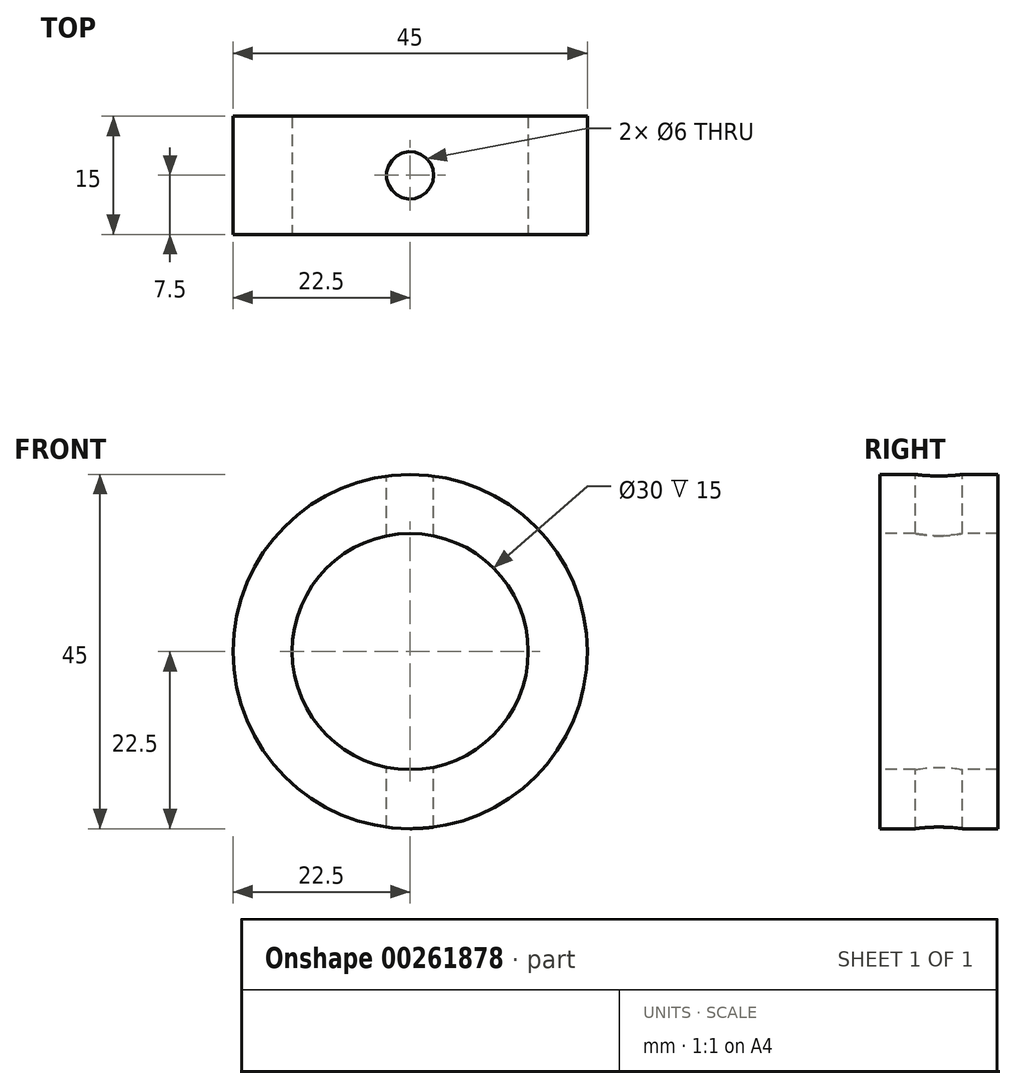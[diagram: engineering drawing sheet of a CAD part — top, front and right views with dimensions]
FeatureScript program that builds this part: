
annotation { "Feature Type Name" : "Feature", "Feature Type Description" : "" }
export const myFeature = defineFeature(function(context is Context, id is Id, definition is map)
    precondition{}
    {
        {
            var Q0;
            Q0=qCreatedBy(makeId("Front.planeOp"),FACE);
            var sketch = newSketch(context, id + "F0", { "sketchPlane" : qUnion([Q0])});
            skCircle(sketch, "E0", {"center": v(0, 0) * mm, "radius": 15 * mm});
            skCircle(sketch, "E1", {"center": v(0, 0) * mm, "radius": 22.5 * mm});
            skSolve(sketch);
        }
        {
            var Q0;
            Q0=makeQuery(id+"F0.imprint","IMPRINT",FACE,{"disambiguationData":[TD([[makeQuery(id+"F0.imprint","IMPRINT",EDGE,{"derivedFrom":sQuery(id+"F0.wireOp",EDGE,"E0")}),1.0]])]});
            var Q1;
            Q1=makeQuery(id+"F0.imprint","IMPRINT",FACE,{"disambiguationData":[TD([[makeQuery(id+"F0.imprint","IMPRINT",EDGE,{"derivedFrom":sQuery(id+"F0.wireOp",EDGE,"E0")}),-1.0]])]});
            extrude(context, id + "F1", {"entities" : qUnion([Q0, Q1]), "oppositeDirection" : true, "depth" : 15 * mm});
        }
        {
            var Q0;
            Q0=makeQuery(id+"F0.imprint","IMPRINT",FACE,{"disambiguationData":[TD([[makeQuery(id+"F0.imprint","IMPRINT",EDGE,{"derivedFrom":sQuery(id+"F0.wireOp",EDGE,"E0")}),1.0]])]});
            extrude(context, id + "F2", {"entities" : qUnion([Q0]), "operationType" : NewBodyOperationType.REMOVE, "endBound" : BoundingType.THROUGH_ALL, "oppositeDirection" : true, "depth" : 25 * mm});
        }
        {
            var Q0;
            Q0=qCreatedBy(makeId("Top.planeOp"),FACE);
            var sketch = newSketch(context, id + "F3", { "sketchPlane" : qUnion([Q0])});
            skCircle(sketch, "E2", {"center": v(0, 7.5) * mm, "radius": 3 * mm});
            skSolve(sketch);
        }
        {
            var Q0;
            Q0 = qSketchRegion(id + "F3", true);
            extrude(context, id + "F4", {"entities" : qUnion([Q0]), "operationType" : NewBodyOperationType.REMOVE, "endBound" : BoundingType.SYMMETRIC, "oppositeDirection" : true, "depth" : 50 * mm});
        }
    });
